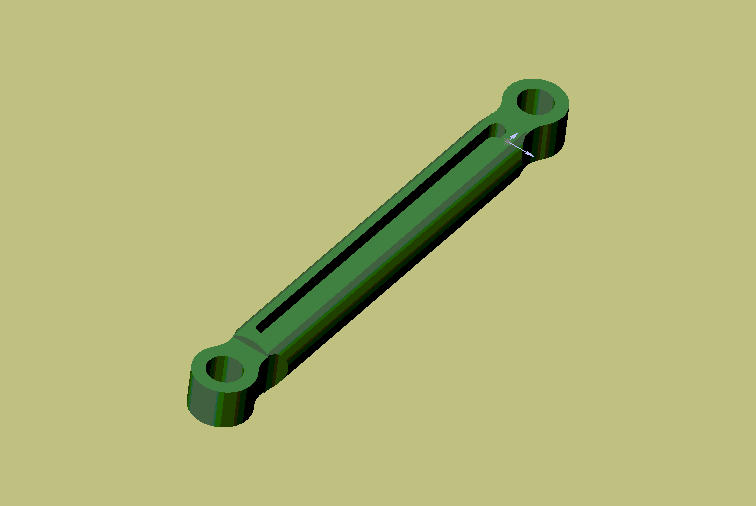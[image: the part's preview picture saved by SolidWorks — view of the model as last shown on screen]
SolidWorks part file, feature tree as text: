
SOLIDWORKS PART (.sldprt)
format: sldprt  version: not decoded by parser v0  size: 181,248 bytes
history: native  units: mm
features: sketch x8, plane x4, mirror x3, extrude x2, cut_extrude x2, material x1 (+8 scaffold rows collapsed)
feature tree (28):
  scaffold x8  (default folders/planes/origin — collapsed)
  material  "Matériau <non spécifié>"
  plane  "Plane1"
  plane  "Plane2"
  plane  "Plane3"
  sketch  "Esquisse1"  dims[c1.D2=7.0mm c1.D1=4.5mm c1.D3=~10.965856mm c2.D3=55.0deg c2.D4=7.0mm]
  extrude  "Base-Extrusion"  Depth=5mm
  sketch  "Esquisse2"  dims[c1.D3=7.0mm c1.D1=12.5mm c2.D1=55.0deg c2.D2=7.0mm]
  sketch  "Esquisse3"  dims[D1=7.0mm]
  extrude  "Boss.-Extru.1"  Depth=45mm
  cut_extrude  "Enlèv. mat.-Extru.1"  Depth=47mm
  plane  "Plan1"  Offset=22.5mm
  mirror  "Symétrie2"
  sketch  "Esquisse4"  dims[D1=4.0mm D2=4.0mm]
  mirror  "Enlèv. mat.-Extru.2"
  sketch  "Esquisse5"
  sketch  "Esquisse6"
  sketch  "Esquisse11"  dims[D1=2.0mm D2=7.0mm D3=7.0mm]
  mirror  "Enlèv. mat.-Extru.3"
  sketch  "Esquisse12"  dims[D1=2.0mm D2=7.0mm D3=7.0mm]
  cut_extrude  "Boss.-Extru.2"  Depth=3mm
decode coverage: 10 of 15 modeling features carry decoded parameters
note: ~ marks probable driven/reference dimensions
note: suppression state not decoded; provenance and decode notes live in map.json
